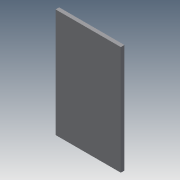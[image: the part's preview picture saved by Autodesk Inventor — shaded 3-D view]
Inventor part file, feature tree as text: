
AUTODESK INVENTOR PART (.ipt)
format: ipt  version: 2015 (Build 190159000, 159)  size: 71,168 bytes
history: native  units: mm
features: extrude x1, sketch x1
ambient origin geometry x8: Origin, YZ Plane, XZ Plane, XY Plane, X Axis, Y Axis, Z Axis, Center Point
bodies: Solid1 (feature_tree)
feature tree (2):
  extrude  "Extrusion1"  Depth=300.0mm
  sketch  "Sketch1"  dims[d0=180.0mm d1=300.0mm d2=10.0mm d3=0.0mm]
